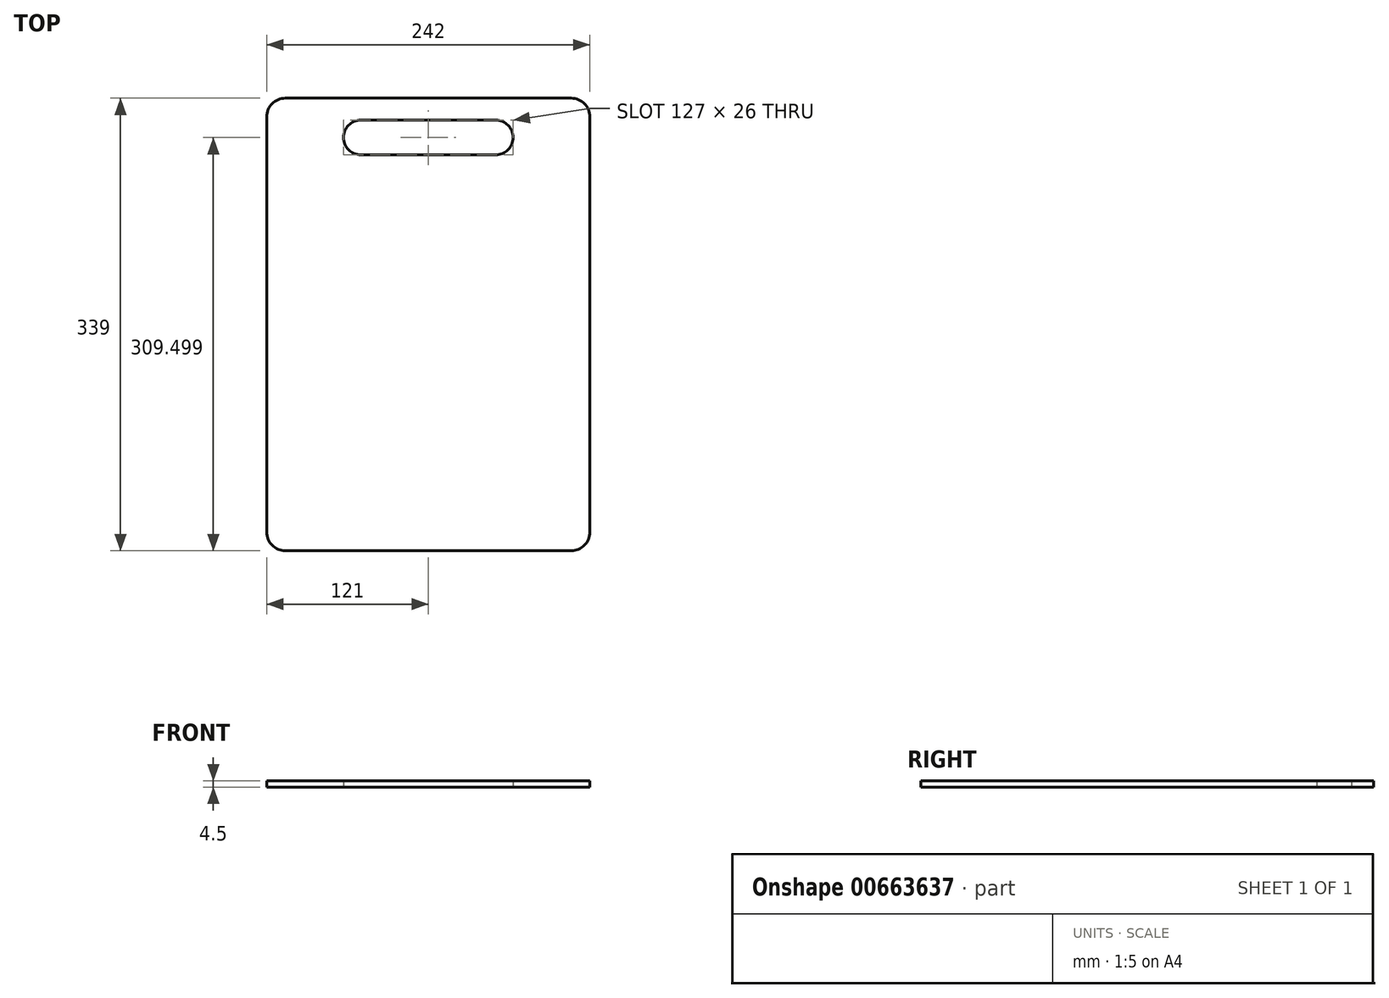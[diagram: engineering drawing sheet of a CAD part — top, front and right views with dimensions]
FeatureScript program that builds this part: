
annotation { "Feature Type Name" : "Feature", "Feature Type Description" : "" }
export const myFeature = defineFeature(function(context is Context, id is Id, definition is map)
    precondition{}
    {
        {
            var Q0;
            Q0=qCreatedBy(makeId("Top.planeOp"),FACE);
            var sketch = newSketch(context, id + "F0", { "sketchPlane" : qUnion([Q0])});
            skLineSegment(sketch, "E0.bottom", {"start": v(-109.12, 146.8) * mm, "end": v(104.88, 146.8) * mm});
            skLineSegment(sketch, "E0.top", {"start": v(-109.12, -192.2) * mm, "end": v(104.88, -192.2) * mm});
            skLineSegment(sketch, "E0.left", {"start": v(-123.12, 132.8) * mm, "end": v(-123.12, -178.2) * mm});
            skLineSegment(sketch, "E0.right", {"start": v(118.88, 132.8) * mm, "end": v(118.88, -178.2) * mm});
            skPoint(sketch, "E1.visualSharp", {"position": v(-123.12, 146.8) * mm});
            skArc(sketch, "E1.filletArc", {"start": v(-109.12, 146.8) * mm, "mid": v(-119.02, 142.7) * mm, "end": v(-123.12, 132.8) * mm});
            skPoint(sketch, "E2.visualSharp", {"position": v(118.88, 146.8) * mm});
            skArc(sketch, "E2.filletArc", {"start": v(118.88, 132.8) * mm, "mid": v(114.78, 142.7) * mm, "end": v(104.88, 146.8) * mm});
            skPoint(sketch, "E3.visualSharp", {"position": v(118.88, -192.2) * mm});
            skArc(sketch, "E3.filletArc", {"start": v(104.88, -192.2) * mm, "mid": v(114.78, -188.1) * mm, "end": v(118.88, -178.2) * mm});
            skPoint(sketch, "E4.visualSharp", {"position": v(-123.12, -192.2) * mm});
            skArc(sketch, "E4.filletArc", {"start": v(-123.12, -178.2) * mm, "mid": v(-119.02, -188.1) * mm, "end": v(-109.12, -192.2) * mm});
            skLineSegment(sketch, "E5.bottom", {"start": v(-52.62, 130.3) * mm, "end": v(48.38, 130.3) * mm});
            skLineSegment(sketch, "E5.top", {"start": v(-52.62, 104.3) * mm, "end": v(48.38, 104.3) * mm});
            skLineSegment(sketch, "E5.left", {"start": v(-65.62, 117.3) * mm, "end": v(-65.62, 117.3) * mm});
            skLineSegment(sketch, "E5.right", {"start": v(61.38, 117.3) * mm, "end": v(61.38, 117.3) * mm});
            skPoint(sketch, "E6", {"position": v(0, 146.8) * mm});
            skPoint(sketch, "E7", {"position": v(-2.12, 104.3) * mm});
            skPoint(sketch, "E8.visualSharp", {"position": v(-65.62, 130.3) * mm});
            skArc(sketch, "E8.filletArc", {"start": v(-52.62, 130.3) * mm, "mid": v(-61.81, 126.5) * mm, "end": v(-65.62, 117.3) * mm});
            skPoint(sketch, "E9.visualSharp", {"position": v(-65.62, 104.3) * mm});
            skArc(sketch, "E9.filletArc", {"start": v(-65.62, 117.3) * mm, "mid": v(-61.81, 108.12) * mm, "end": v(-52.62, 104.3) * mm});
            skPoint(sketch, "E10.visualSharp", {"position": v(61.38, 104.3) * mm});
            skArc(sketch, "E10.filletArc", {"start": v(48.38, 104.3) * mm, "mid": v(57.57, 108.12) * mm, "end": v(61.38, 117.3) * mm});
            skPoint(sketch, "E11.visualSharp", {"position": v(61.38, 130.3) * mm});
            skArc(sketch, "E11.filletArc", {"start": v(61.38, 117.3) * mm, "mid": v(57.57, 126.5) * mm, "end": v(48.38, 130.3) * mm});
            skSolve(sketch);
        }
        {
            var Q0;
            Q0 = qSketchRegion(id + "F0", true);
            extrude(context, id + "F1", {"entities" : qUnion([Q0]), "depth" : 4.5 * mm, "offsetDistance" : 25 * mm});
        }
    });
